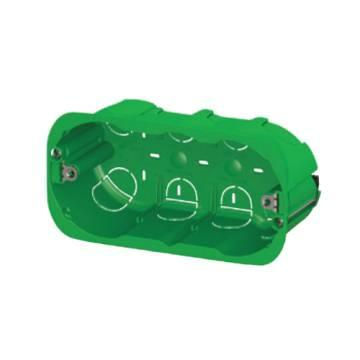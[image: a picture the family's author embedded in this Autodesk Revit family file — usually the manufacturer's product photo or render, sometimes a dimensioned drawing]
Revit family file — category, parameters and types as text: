
# Revit family: Building-ContenitoriIncasso-GEWISS-24SC-GREENWALL-SCATOLE-INCASSO_4P
name_source: partatom
category: Apparecchi elettrici
revit_build: Autodesk Revit 2016 (Build: 20161004_0715(x64)
units: mm (PartAtom-declared; Revit-internal decimal feet)

## family parameters
Condiviso = Sì
Host = Superficie
Mantenere orientamento annotazione = Sì
Numero OmniClass = 23.80.30.14.24
Punto di calcolo locali = Sì
Quota connettore circolare = Usa diametro
Taglio con vuoti quando caricato = Sì
Tipo di parte = Normale
Titolo OmniClass = Junction Boxes

## types (1)
- GW24404PM - Halogen free - 4P
    Caratteristiche = Halogen free
    Catalogo = BUILDING
    Catalogo Serie = 24SC
    Codice EAN = 8011564801929
    Codice Electrocod = 0210
    Descrizione = SCATOLA 4P.PARETI MOBILI-LEGGERE GREEN
    Descrizione: = 4 posti
    Dim. esterne BxHxP (mm) = 133x73x50
    Elementi acciaio = GEWISS - Elementi acciaio
    Glow Wire Test = 850°C
    Grado di protezione = IP40
    IDF = 50be33b2-a635-4952-8c9f-674dcb1e5a96
    IDT = ced4c316-61fc-4ec6-8ed7-dfe497302916
    Immagine tipo = GW24404PM.jpg
    Installazione = Incasso
    Interasse fissaggio supporti = 108,5MM
    Modello = GW24404PM
    N. moduli SYSTEM = 4 posti
    Per Pareti = Cartongesso
    Predisposizione scomparti = 2
    Produttore = GEWISS S.p.A.
    Prospetto di default = 1219.2 mm  [stored 4 ft]
    Resistenza agli urti = IK07
    SEO = Scatola
    Scatola = GEWISS - scatola a incasso
    Scheda Tecnica = https://www.gewiss.com
    Temperatura di impiego = -15 +60 °C
    Termopressione con biglia = 70 °C
    Tipo Materiale = Halogen free secondo norma EN 50267-2-2
    Tipo: = Alta capienza
    URL = https://www.gewiss.com
    Versione file RFA = 19.0

note: [stored X ft] marks values corroborated as IEEE doubles in the binary element streams (Revit-internal decimal feet)

## geometry (parser evidence)
native form markers: Blend x2, Sweep x3
no freeform markers — native parametric forms only
